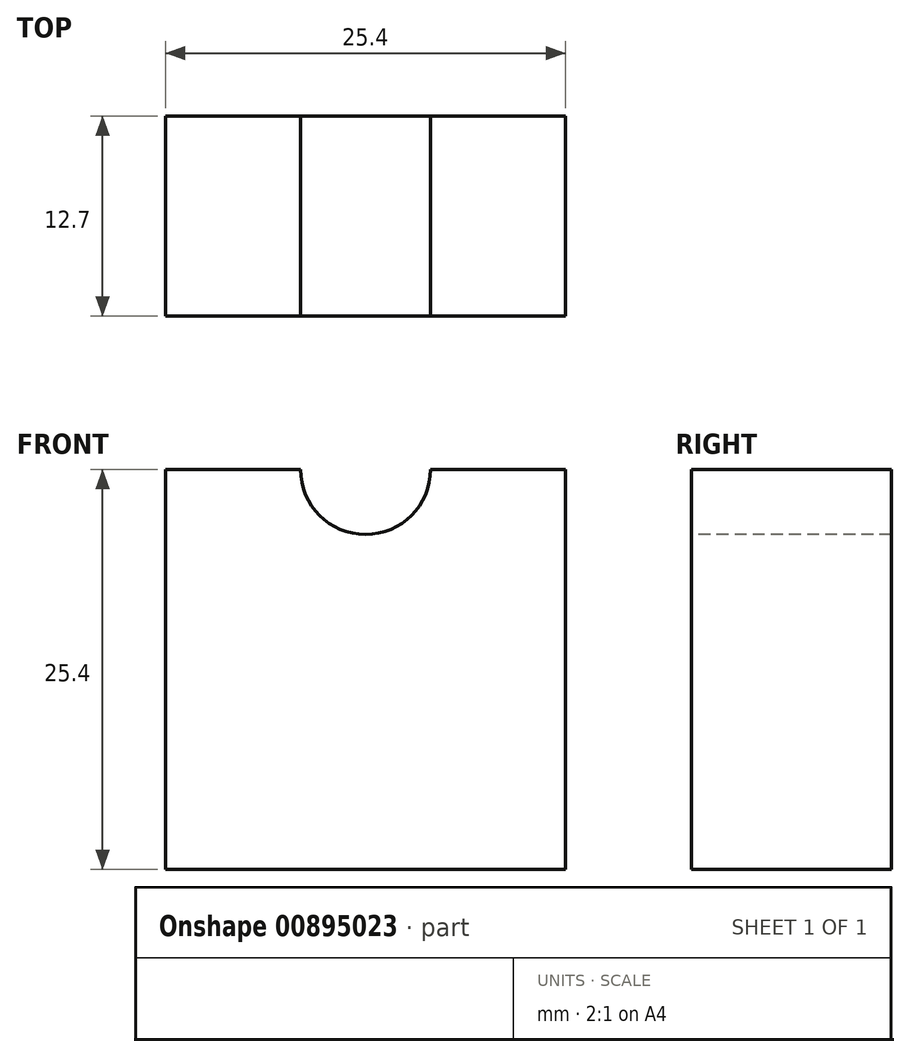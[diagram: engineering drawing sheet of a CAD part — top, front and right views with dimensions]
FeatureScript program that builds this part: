
annotation { "Feature Type Name" : "Feature", "Feature Type Description" : "" }
export const myFeature = defineFeature(function(context is Context, id is Id, definition is map)
    precondition{}
    {
        {
            var Q0;
            Q0=qCreatedBy(makeId("Top.planeOp"),FACE);
            var sketch = newSketch(context, id + "F0", { "sketchPlane" : qUnion([Q0])});
            skLineSegment(sketch, "E0.bottom", {"start": v(-2.89, 22.78) * mm, "end": v(22.51, 22.78) * mm});
            skLineSegment(sketch, "E0.top", {"start": v(-2.89, 10.08) * mm, "end": v(22.51, 10.08) * mm});
            skLineSegment(sketch, "E0.left", {"start": v(-2.89, 22.78) * mm, "end": v(-2.89, 10.08) * mm});
            skLineSegment(sketch, "E0.right", {"start": v(22.51, 22.78) * mm, "end": v(22.51, 10.08) * mm});
            skSolve(sketch);
        }
        {
            var Q0;
            Q0=qSketchRegion(id+"F0",true);
            extrude(context, id + "F1", {"entities" : qUnion([Q0]), "depth" : 25.4 * mm, "offsetDistance" : 25.4 * mm});
        }
        {
            var Q0;
            Q0=makeQuery(id+"F1.opExtrude","SWEPT_FACE",FACE,{"disambiguationData":[OSD([sQuery(id+"F0.wireOp",EDGE,"E0.top")])]});
            var sketch = newSketch(context, id + "F2", { "sketchPlane" : qUnion([Q0])});
            skCircle(sketch, "E1", {"center": v(9.81, 25.4) * mm, "radius": 4.13 * mm});
            skPoint(sketch, "E1.centerSnap0", {"position": v(9.81, 25.4) * mm});
            skSolve(sketch);
        }
        {
            var Q0;
            Q0=qSketchRegion(id+"F2",true);
            extrude(context, id + "F3", {"entities" : qUnion([Q0]), "operationType" : NewBodyOperationType.REMOVE, "oppositeDirection" : true, "depth" : 25.4 * mm, "offsetDistance" : 25.4 * mm});
        }
    });
